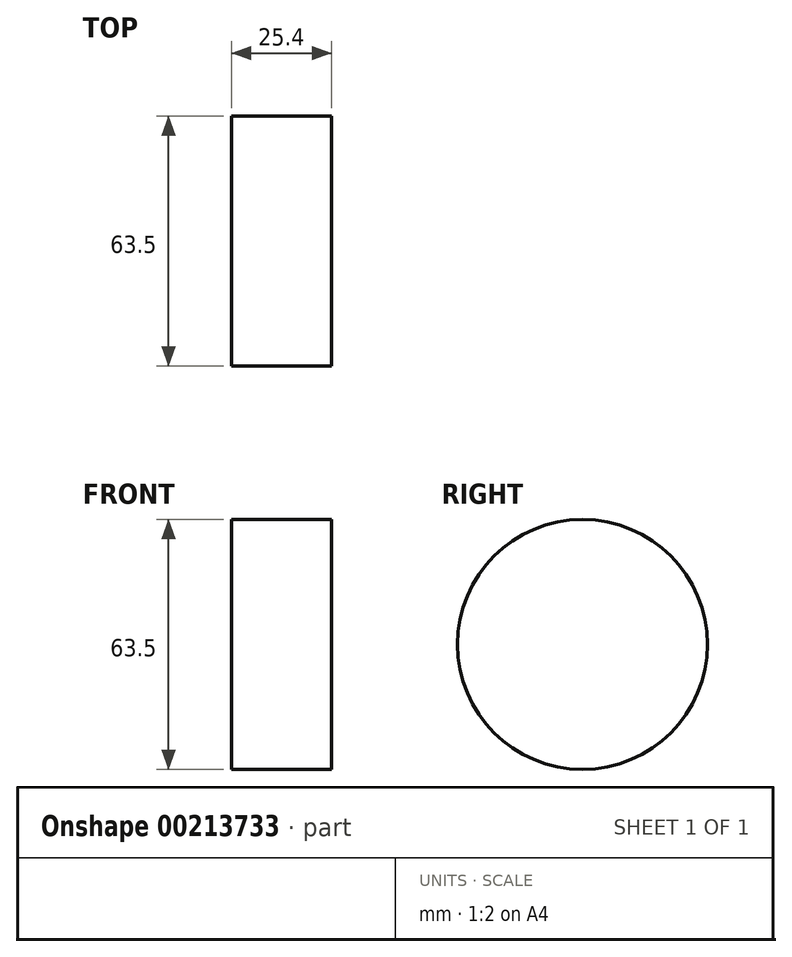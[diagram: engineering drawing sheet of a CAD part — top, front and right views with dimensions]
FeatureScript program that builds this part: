
annotation { "Feature Type Name" : "Feature", "Feature Type Description" : "" }
export const myFeature = defineFeature(function(context is Context, id is Id, definition is map)
    precondition{}
    {
        {
            var Q0;
            Q0=qCreatedBy(makeId("Right.planeOp"),FACE);
            var sketch = newSketch(context, id + "F0", { "sketchPlane" : qUnion([Q0])});
            skCircle(sketch, "E0", {"center": v(0, 0) * mm, "radius": 31.75 * mm});
            skSolve(sketch);
        }
        {
            var Q0;
            Q0 = qSketchRegion(id + "F0", true);
            extrude(context, id + "F1", {"entities" : qUnion([Q0]), "depth" : 25.4 * mm});
        }
    });
